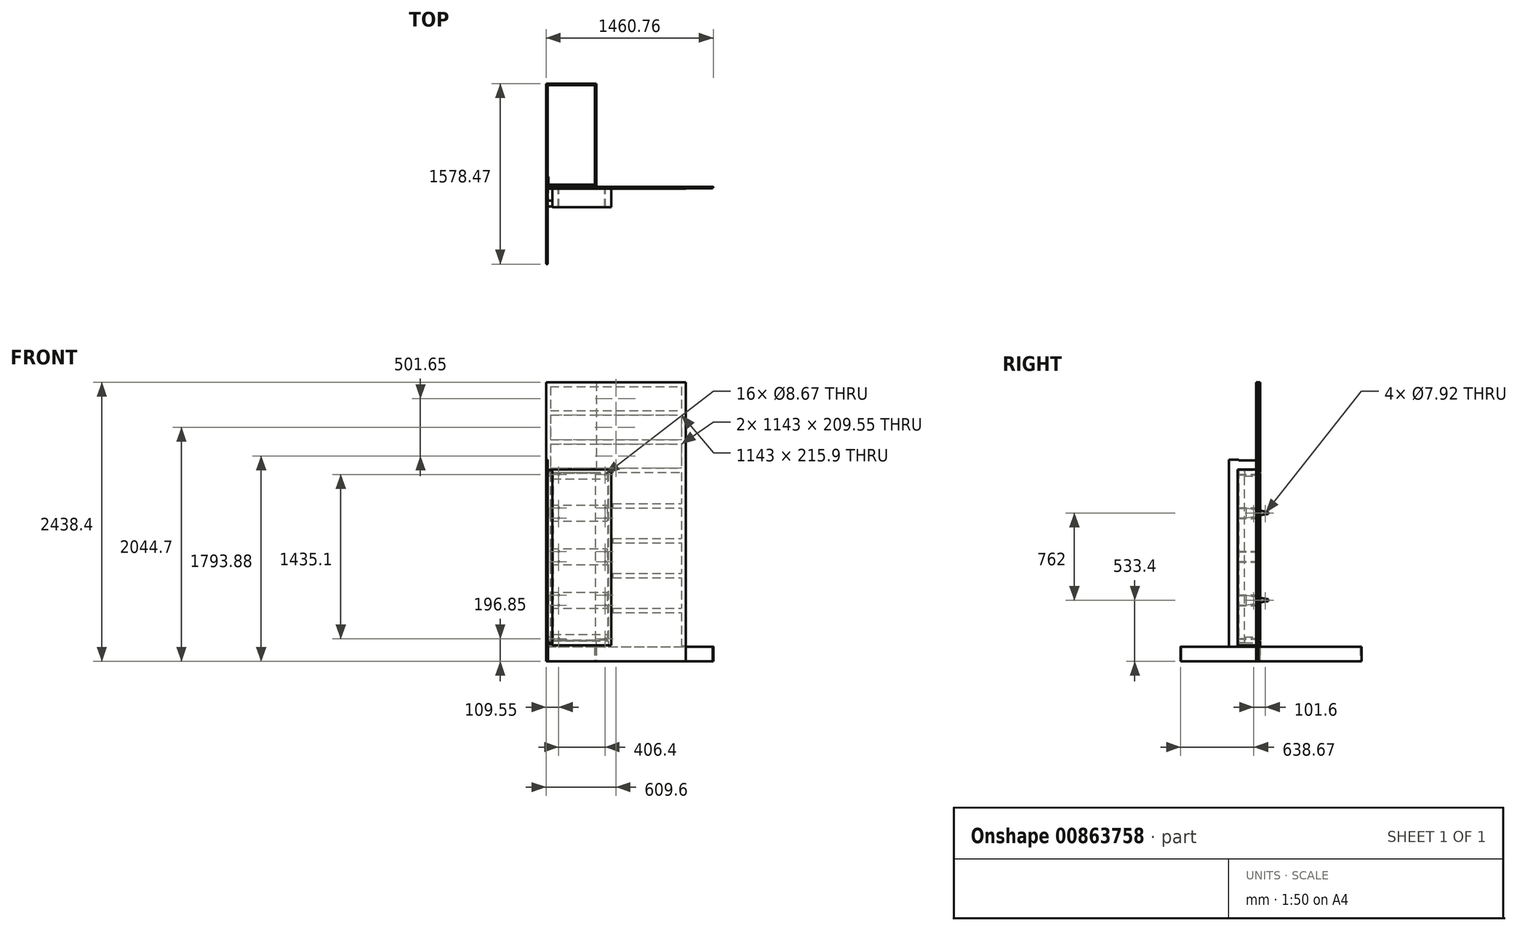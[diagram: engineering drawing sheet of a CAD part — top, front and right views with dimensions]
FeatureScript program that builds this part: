
annotation { "Feature Type Name" : "Feature", "Feature Type Description" : "" }
export const myFeature = defineFeature(function(context is Context, id is Id, definition is map)
    precondition{}
    {
        {
            var Q0;
            Q0=qCreatedBy(makeId("Top.planeOp"),FACE);
            var sketch = newSketch(context, id + "F0", { "sketchPlane" : qUnion([Q0])});
            skLineSegment(sketch, "E0", {"start": v(0, -673.1) * mm, "end": v(0, 901.7) * mm});
            skLineSegment(sketch, "E1", {"start": v(0, 901.7) * mm, "end": v(438.15, 901.7) * mm});
            skLineSegment(sketch, "E2", {"start": v(438.15, 901.7) * mm, "end": v(438.15, 0) * mm});
            skLineSegment(sketch, "E3", {"start": v(438.15, 0) * mm, "end": v(1454.15, 0) * mm});
            skLineSegment(sketch, "E4.0", {"start": v(552.45, 114.3) * mm, "end": v(1454.15, 114.3) * mm});
            skLineSegment(sketch, "E4.1", {"start": v(552.45, 1016) * mm, "end": v(552.45, 114.3) * mm});
            skLineSegment(sketch, "E4.2", {"start": v(-114.3, 1016) * mm, "end": v(552.45, 1016) * mm});
            skLineSegment(sketch, "E4.3", {"start": v(-114.3, -673.1) * mm, "end": v(-114.3, 1016) * mm});
            skLineSegment(sketch, "E5.0", {"start": v(425.45, -12.7) * mm, "end": v(1454.15, -12.7) * mm});
            skLineSegment(sketch, "E5.1", {"start": v(425.45, 889) * mm, "end": v(425.45, -12.7) * mm});
            skLineSegment(sketch, "E5.2", {"start": v(12.7, 889) * mm, "end": v(425.45, 889) * mm});
            skLineSegment(sketch, "E5.3", {"start": v(12.7, -673.1) * mm, "end": v(12.7, 889) * mm});
            skFitSpline(sketch, "E6", {"points": [v(-114.3, -673.1) * mm, v(0, -673.1) * mm, v(12.7, -673.1) * mm], "startDerivative": vector(215.33, 101.54) * mm, "endDerivative": vector(15.02, 74.43) * mm});
            skFitSpline(sketch, "E7", {"points": [v(1454.15, 114.3) * mm, v(1454.15, 0) * mm, v(1454.15, -12.7) * mm], "startDerivative": vector(-157.16, -195.04) * mm, "endDerivative": vector(-135.93, -152.4) * mm});
            skLineSegment(sketch, "E8.bottom", {"start": v(30.7, -669.3) * mm, "end": v(1447.96, -669.3) * mm, "construction": true});
            skLineSegment(sketch, "E8.top", {"start": v(30.7, -660.4) * mm, "end": v(1447.96, -660.4) * mm, "construction": true});
            skLineSegment(sketch, "E8.left", {"start": v(30.7, -669.3) * mm, "end": v(30.7, -660.4) * mm, "construction": true});
            skLineSegment(sketch, "E8.right", {"start": v(1447.96, -669.3) * mm, "end": v(1447.96, -660.4) * mm, "construction": true});
            skLineSegment(sketch, "E9", {"start": v(27.37, -457.2) * mm, "end": v(1426.84, -457.2) * mm, "construction": true});
            skText(sketch, "E10", { "text": "Clothes\n", "fontName": "OpenSans-Regular.ttf"});
            skText(sketch, "E11", { "text": "Shelf", "fontName": "OpenSans-Regular.ttf"});
            skLineSegment(sketch, "E12", {"start": v(-114.3, 584.2) * mm, "end": v(0, 584.2) * mm, "construction": true});
            skLineSegment(sketch, "E13", {"start": v(-114.3, 177.8) * mm, "end": v(0, 177.8) * mm, "construction": true});
            skLineSegment(sketch, "E14", {"start": v(438.15, 556.05) * mm, "end": v(552.45, 556.05) * mm, "construction": true});
            skLineSegment(sketch, "E15", {"start": v(958.85, 0) * mm, "end": v(958.85, 114.3) * mm, "construction": true});
            const initialGuessF0  = {"E10": [1.1723, -0.49137, 1, 0, 0.01667], "E11": [1.16785, -0.64477, 1, 0, 0.02]};
            skSetInitialGuess(sketch, initialGuessF0);
            skSolve(sketch);
        }
        {
            var Q0;
            Q0=qCreatedBy(makeId("Front.planeOp"),FACE);
            var sketch = newSketch(context, id + "F1", { "sketchPlane" : qUnion([Q0])});
            skLineSegment(sketch, "E16.bottom", {"start": v(0, 0) * mm, "end": v(12.7, 0) * mm, "construction": true});
            skLineSegment(sketch, "E16.top", {"start": v(0, 127) * mm, "end": v(12.7, 127) * mm, "construction": true});
            skLineSegment(sketch, "E16.left", {"start": v(0, 0) * mm, "end": v(0, 127) * mm, "construction": true});
            skLineSegment(sketch, "E16.right", {"start": v(12.7, 0) * mm, "end": v(12.7, 127) * mm, "construction": true});
            skLineSegment(sketch, "E17.bottom", {"start": v(438.15, 0) * mm, "end": v(425.45, 0) * mm, "construction": true});
            skLineSegment(sketch, "E17.top", {"start": v(438.15, 127) * mm, "end": v(425.45, 127) * mm, "construction": true});
            skLineSegment(sketch, "E17.left", {"start": v(438.15, 0) * mm, "end": v(438.15, 127) * mm, "construction": true});
            skLineSegment(sketch, "E17.right", {"start": v(425.45, 0) * mm, "end": v(425.45, 127) * mm, "construction": true});
            skLineSegment(sketch, "E18.bottom", {"start": v(0, 0) * mm, "end": v(438.15, 0) * mm, "construction": true});
            skLineSegment(sketch, "E18.top", {"start": v(0, 2438.4) * mm, "end": v(438.15, 2438.4) * mm, "construction": true});
            skLineSegment(sketch, "E18.left", {"start": v(0, 0) * mm, "end": v(0, 2438.4) * mm, "construction": true});
            skLineSegment(sketch, "E18.right", {"start": v(438.15, 0) * mm, "end": v(438.15, 2438.4) * mm, "construction": true});
            skLineSegment(sketch, "E19", {"start": v(958.85, 0) * mm, "end": v(958.85, 2438.4) * mm, "construction": true});
            skLineSegment(sketch, "E20", {"start": v(565.15, 0) * mm, "end": v(565.15, 2438.4) * mm, "construction": true});
            skSolve(sketch);
        }
        {
            var Q0;
            {var subQ2=sQuery(id+"F0.wireOp",EDGE,"E0");Q0=makeQuery(id+"F0.imprint","IMPRINT",FACE,{"disambiguationData":[TD([[makeQuery(id+"F0.imprint","IMPRINT",EDGE,{"derivedFrom":subQ2}),-1.0]])]});}
            var Q1;
            Q1=sQuery(id+"F0.wireOp",EDGE,"E0");
            var Q2;
            Q2=sQuery(id+"F0.wireOp",EDGE,"E1");
            var Q3;
            Q3=sQuery(id+"F0.wireOp",EDGE,"E2");
            var Q4;
            Q4=sQuery(id+"F0.wireOp",EDGE,"E5.1");
            var Q5;
            Q5=sQuery(id+"F0.wireOp",EDGE,"E5.2");
            var Q6;
            Q6=sQuery(id+"F0.wireOp",EDGE,"E5.3");
            var Q7;
            Q7=sQuery(id+"F0.wireOp",EDGE,"E3");
            var Q8;
            Q8=sQuery(id+"F0.wireOp",EDGE,"E5.0");
            extrude(context, id + "F2", {"entities" : qUnion([Q0]), "surfaceEntities" : qUnion([Q1, Q2, Q3, Q4, Q5, Q6, Q7, Q8]), "depth" : 127 * mm, "offsetDistance" : 25.4 * mm});
        }
        {
            var Q0;
            Q0=qCreatedBy(makeId("Front.planeOp"),FACE);
            cPlane(context, id + "F3", {"entities" : qUnion([Q0]), "cplaneType" : CPlaneType.OFFSET, "offset" : 17.45 * mm, "width" : 152.4 * mm, "height" : 152.4 * mm});
        }
        {
            var Q0;
            Q0=qCreatedBy(id+"F3.planeOp",FACE);
            var sketch = newSketch(context, id + "F4", { "sketchPlane" : qUnion([Q0])});
            skLineSegment(sketch, "E21.bottom", {"start": v(55.58, 139.7) * mm, "end": v(569.93, 139.7) * mm});
            skLineSegment(sketch, "E21.top", {"start": v(55.58, 1676.4) * mm, "end": v(569.93, 1676.4) * mm});
            skLineSegment(sketch, "E21.left", {"start": v(55.58, 139.7) * mm, "end": v(55.58, 1676.4) * mm});
            skLineSegment(sketch, "E21.right", {"start": v(569.93, 139.7) * mm, "end": v(569.93, 1676.4) * mm});
            skLineSegment(sketch, "E22", {"start": v(55.58, 1295.4) * mm, "end": v(569.93, 1295.4) * mm});
            skLineSegment(sketch, "E23", {"start": v(55.58, 914.4) * mm, "end": v(569.93, 914.4) * mm});
            skLineSegment(sketch, "E24", {"start": v(55.58, 533.4) * mm, "end": v(569.93, 533.4) * mm});
            skLineSegment(sketch, "E25", {"start": v(55.58, 152.4) * mm, "end": v(569.93, 152.4) * mm, "construction": true});
            skCircle(sketch, "E26", {"center": v(109.55, 1631.95) * mm, "radius": 4.33 * mm});
            skCircle(sketch, "E27", {"center": v(109.55, 1339.85) * mm, "radius": 4.33 * mm});
            skCircle(sketch, "E28", {"center": v(109.55, 1250.95) * mm, "radius": 4.33 * mm});
            skCircle(sketch, "E29", {"center": v(109.55, 958.85) * mm, "radius": 4.33 * mm});
            skCircle(sketch, "E30", {"center": v(109.55, 869.95) * mm, "radius": 4.33 * mm});
            skCircle(sketch, "E31", {"center": v(109.55, 577.85) * mm, "radius": 4.33 * mm});
            skCircle(sketch, "E32", {"center": v(109.55, 488.95) * mm, "radius": 4.33 * mm});
            skCircle(sketch, "E33", {"center": v(109.55, 196.85) * mm, "radius": 4.33 * mm});
            skLineSegment(sketch, "E34", {"start": v(109.55, 1631.95) * mm, "end": v(109.55, 196.85) * mm, "construction": true});
            skCircle(sketch, "E35", {"center": v(515.95, 1631.95) * mm, "radius": 4.33 * mm});
            skCircle(sketch, "E36", {"center": v(515.95, 1339.85) * mm, "radius": 4.33 * mm});
            skCircle(sketch, "E37", {"center": v(515.95, 1250.95) * mm, "radius": 4.33 * mm});
            skCircle(sketch, "E38", {"center": v(515.95, 958.85) * mm, "radius": 4.33 * mm});
            skCircle(sketch, "E39", {"center": v(515.95, 869.95) * mm, "radius": 4.33 * mm});
            skCircle(sketch, "E40", {"center": v(515.95, 577.85) * mm, "radius": 4.33 * mm});
            skCircle(sketch, "E41", {"center": v(515.95, 488.95) * mm, "radius": 4.33 * mm});
            skCircle(sketch, "E42", {"center": v(515.95, 196.85) * mm, "radius": 4.33 * mm});
            skLineSegment(sketch, "E43", {"start": v(515.95, 1631.95) * mm, "end": v(515.95, 196.85) * mm, "construction": true});
            skLineSegment(sketch, "E44", {"start": v(109.55, 1631.95) * mm, "end": v(515.95, 1631.95) * mm, "construction": true});
            skLineSegment(sketch, "E45", {"start": v(109.55, 196.85) * mm, "end": v(515.95, 196.85) * mm, "construction": true});
            skLineSegment(sketch, "E46", {"start": v(109.55, 488.95) * mm, "end": v(515.95, 488.95) * mm, "construction": true});
            skLineSegment(sketch, "E47", {"start": v(109.55, 577.85) * mm, "end": v(515.95, 577.85) * mm, "construction": true});
            skLineSegment(sketch, "E48", {"start": v(109.55, 869.95) * mm, "end": v(515.95, 869.95) * mm, "construction": true});
            skLineSegment(sketch, "E49", {"start": v(109.55, 958.85) * mm, "end": v(515.95, 958.85) * mm, "construction": true});
            skLineSegment(sketch, "E50", {"start": v(109.55, 1250.95) * mm, "end": v(515.95, 1250.95) * mm, "construction": true});
            skLineSegment(sketch, "E51", {"start": v(109.55, 1339.85) * mm, "end": v(515.95, 1339.85) * mm, "construction": true});
            skSolve(sketch);
        }
        {
            var Q0;
            Q0=qCreatedBy(makeId("Front.planeOp"),FACE);
            var Q1;
            Q1 = qBodyType(qCreatedBy(id + "F13" ,EDGE), BodyType.WIRE);
            cPlane(context, id + "F5", {"entities" : qUnion([Q0, Q1]), "cplaneType" : CPlaneType.OFFSET, "offset" : 12.7 * mm, "width" : 152.4 * mm, "height" : 152.4 * mm});
        }
        {
            var Q0;
            Q0=qCreatedBy(id+"F5.planeOp",FACE);
            var sketch = newSketch(context, id + "F6", { "sketchPlane" : qUnion([Q0])});
            skLineSegment(sketch, "E52", {"start": v(3.17, 177.8) * mm, "end": v(3.18, 130.18) * mm});
            skLineSegment(sketch, "E53", {"start": v(3.18, 130.18) * mm, "end": v(15.87, 130.18) * mm});
            skLineSegment(sketch, "E54", {"start": v(15.87, 130.18) * mm, "end": v(15.88, 0) * mm});
            skLineSegment(sketch, "E55", {"start": v(15.87, 0) * mm, "end": v(1219.2, 0) * mm});
            skLineSegment(sketch, "E56", {"start": v(1219.2, 0) * mm, "end": v(1219.2, 2438.4) * mm});
            skLineSegment(sketch, "E57", {"start": v(1219.2, 2438.4) * mm, "end": v(0, 2438.4) * mm});
            skLineSegment(sketch, "E58", {"start": v(0, 2438.4) * mm, "end": v(0, 1651) * mm});
            skLineSegment(sketch, "E59", {"start": v(0, 1651) * mm, "end": v(544.53, 1651) * mm});
            skLineSegment(sketch, "E60", {"start": v(544.53, 1651) * mm, "end": v(544.53, 177.8) * mm});
            skLineSegment(sketch, "E61", {"start": v(544.53, 177.8) * mm, "end": v(3.17, 177.8) * mm});
            skSolve(sketch);
        }
        {
            var Q0;
            Q0=makeQuery(id+"F6.imprint","IMPRINT",FACE,{"disambiguationData":[TD([[makeQuery(id+"F6.imprint","IMPRINT",EDGE,{"derivedFrom":sQuery(id+"F6.wireOp",EDGE,"E52")}),1.0]])]});
            extrude(context, id + "F7", {"entities" : qUnion([Q0]), "depth" : 4.75 * mm, "offsetDistance" : 25.4 * mm});
        }
        {
            var Q0;
            Q0=qCreatedBy(id+"F5.planeOp",FACE);
            var sketch = newSketch(context, id + "F8", { "sketchPlane" : qUnion([Q0])});
            skLineSegment(sketch, "E62.bottom", {"start": v(1219.2, 2438.4) * mm, "end": v(1181.1, 2438.4) * mm});
            skLineSegment(sketch, "E62.top", {"start": v(1219.2, 133.35) * mm, "end": v(1181.1, 133.35) * mm});
            skLineSegment(sketch, "E62.left", {"start": v(1219.2, 2438.4) * mm, "end": v(1219.2, 133.35) * mm});
            skLineSegment(sketch, "E62.right", {"start": v(1181.1, 2438.4) * mm, "end": v(1181.1, 133.35) * mm});
            skLineSegment(sketch, "E63.bottom", {"start": v(38.1, 1689.1) * mm, "end": v(1181.1, 1689.1) * mm});
            skLineSegment(sketch, "E63.top", {"start": v(38.1, 1651) * mm, "end": v(1181.1, 1651) * mm});
            skLineSegment(sketch, "E63.right", {"start": v(1181.1, 1689.1) * mm, "end": v(1181.1, 1651) * mm});
            skLineSegment(sketch, "E64.bottom", {"start": v(38.1, 1936.75) * mm, "end": v(1181.1, 1936.75) * mm});
            skLineSegment(sketch, "E64.top", {"start": v(38.1, 1898.65) * mm, "end": v(1181.1, 1898.65) * mm});
            skLineSegment(sketch, "E64.left", {"start": v(38.1, 1936.75) * mm, "end": v(38.1, 1898.65) * mm});
            skLineSegment(sketch, "E64.right", {"start": v(1181.1, 1936.75) * mm, "end": v(1181.1, 1898.65) * mm});
            skLineSegment(sketch, "E65.bottom", {"start": v(38.1, 2190.75) * mm, "end": v(1181.1, 2190.75) * mm});
            skLineSegment(sketch, "E65.top", {"start": v(38.1, 2152.65) * mm, "end": v(1181.1, 2152.65) * mm});
            skLineSegment(sketch, "E65.left", {"start": v(38.1, 2190.75) * mm, "end": v(38.1, 2152.65) * mm});
            skLineSegment(sketch, "E65.right", {"start": v(1181.1, 2190.75) * mm, "end": v(1181.1, 2152.65) * mm});
            skLineSegment(sketch, "E66.bottom", {"start": v(38.1, 2438.4) * mm, "end": v(1181.1, 2438.4) * mm});
            skLineSegment(sketch, "E66.top", {"start": v(38.1, 2400.3) * mm, "end": v(1181.1, 2400.3) * mm});
            skLineSegment(sketch, "E66.left", {"start": v(38.1, 2438.4) * mm, "end": v(38.1, 2400.3) * mm});
            skLineSegment(sketch, "E66.right", {"start": v(1181.1, 2438.4) * mm, "end": v(1181.1, 2400.3) * mm});
            skLineSegment(sketch, "E67.bottom", {"start": v(582.63, 1377.95) * mm, "end": v(1181.1, 1377.95) * mm});
            skLineSegment(sketch, "E67.top", {"start": v(582.63, 1339.85) * mm, "end": v(1181.1, 1339.85) * mm});
            skLineSegment(sketch, "E67.left", {"start": v(582.63, 1377.95) * mm, "end": v(582.63, 1339.85) * mm});
            skLineSegment(sketch, "E67.right", {"start": v(1181.1, 1377.95) * mm, "end": v(1181.1, 1339.85) * mm});
            skLineSegment(sketch, "E68.bottom", {"start": v(544.53, 1651) * mm, "end": v(582.63, 1651) * mm});
            skLineSegment(sketch, "E68.top", {"start": v(544.53, 133.35) * mm, "end": v(582.63, 133.35) * mm});
            skLineSegment(sketch, "E68.left", {"start": v(544.53, 1651) * mm, "end": v(544.53, 133.35) * mm});
            skLineSegment(sketch, "E68.right", {"start": v(582.63, 1651) * mm, "end": v(582.63, 133.35) * mm});
            skLineSegment(sketch, "E69.bottom", {"start": v(582.63, 1073.15) * mm, "end": v(1181.1, 1073.15) * mm});
            skLineSegment(sketch, "E69.top", {"start": v(582.63, 1035.05) * mm, "end": v(1181.1, 1035.05) * mm});
            skLineSegment(sketch, "E69.left", {"start": v(582.63, 1073.15) * mm, "end": v(582.63, 1035.05) * mm});
            skLineSegment(sketch, "E69.right", {"start": v(1181.1, 1073.15) * mm, "end": v(1181.1, 1035.05) * mm});
            skLineSegment(sketch, "E70.bottom", {"start": v(582.63, 768.35) * mm, "end": v(1181.1, 768.35) * mm});
            skLineSegment(sketch, "E70.top", {"start": v(582.63, 730.25) * mm, "end": v(1181.1, 730.25) * mm});
            skLineSegment(sketch, "E70.left", {"start": v(582.63, 768.35) * mm, "end": v(582.63, 730.25) * mm});
            skLineSegment(sketch, "E70.right", {"start": v(1181.1, 768.35) * mm, "end": v(1181.1, 730.25) * mm});
            skLineSegment(sketch, "E71.bottom", {"start": v(582.63, 463.55) * mm, "end": v(1181.1, 463.55) * mm});
            skLineSegment(sketch, "E71.top", {"start": v(582.63, 425.45) * mm, "end": v(1181.1, 425.45) * mm});
            skLineSegment(sketch, "E71.left", {"start": v(582.63, 463.55) * mm, "end": v(582.63, 425.45) * mm});
            skLineSegment(sketch, "E71.right", {"start": v(1181.1, 463.55) * mm, "end": v(1181.1, 425.45) * mm});
            skLineSegment(sketch, "E72.bottom", {"start": v(15.88, 127) * mm, "end": v(422.28, 127) * mm});
            skLineSegment(sketch, "E72.top", {"start": v(15.88, 0) * mm, "end": v(422.28, 0) * mm});
            skLineSegment(sketch, "E72.left", {"start": v(15.87, 127) * mm, "end": v(15.87, 0) * mm});
            skLineSegment(sketch, "E72.right", {"start": v(422.28, 127) * mm, "end": v(422.28, 0) * mm});
            skLineSegment(sketch, "E73.bottom", {"start": v(3.18, 177.8) * mm, "end": v(544.53, 177.8) * mm});
            skLineSegment(sketch, "E73.top", {"start": v(3.18, 139.7) * mm, "end": v(544.53, 139.7) * mm});
            skLineSegment(sketch, "E73.left", {"start": v(3.17, 177.8) * mm, "end": v(3.18, 139.7) * mm});
            skLineSegment(sketch, "E73.right", {"start": v(544.53, 177.8) * mm, "end": v(544.53, 139.7) * mm});
            skLineSegment(sketch, "E74.bottom", {"start": v(0, 2438.4) * mm, "end": v(38.1, 2438.4) * mm});
            skLineSegment(sketch, "E74.top", {"start": v(0, 1651) * mm, "end": v(38.1, 1651) * mm});
            skLineSegment(sketch, "E74.left", {"start": v(0, 2438.4) * mm, "end": v(0, 1651) * mm});
            skLineSegment(sketch, "E74.right", {"start": v(38.1, 2438.4) * mm, "end": v(38.1, 1651) * mm});
            skLineSegment(sketch, "E75", {"start": v(38.1, 1689.1) * mm, "end": v(38.1, 1651) * mm});
            skSolve(sketch);
        }
        {
            var Q0;
            Q0=qCreatedBy(makeId("Top.planeOp"),FACE);
            cPlane(context, id + "F9", {"entities" : qUnion([Q0]), "cplaneType" : CPlaneType.OFFSET, "offset" : 1524 * mm, "width" : 152.4 * mm, "height" : 152.4 * mm});
        }
        {
            var Q0;
            Q0=qCreatedBy(id+"F9.planeOp",FACE);
            var sketch = newSketch(context, id + "F10", { "sketchPlane" : qUnion([Q0])});
            skLineSegment(sketch, "E76.bottom", {"start": v(0, -107.95) * mm, "end": v(19.05, -107.95) * mm});
            skLineSegment(sketch, "E76.top", {"start": v(0, 704.85) * mm, "end": v(19.05, 704.85) * mm});
            skLineSegment(sketch, "E76.left", {"start": v(0, -107.95) * mm, "end": v(0, 704.85) * mm});
            skLineSegment(sketch, "E76.right", {"start": v(19.05, -107.95) * mm, "end": v(19.05, 704.85) * mm});
            skLineSegment(sketch, "E77.bottom", {"start": v(19.05, 87.31) * mm, "end": v(21.59, 87.31) * mm});
            skLineSegment(sketch, "E77.top", {"start": v(19.05, -158.75) * mm, "end": v(21.6, -158.75) * mm});
            skLineSegment(sketch, "E77.left", {"start": v(19.05, 87.31) * mm, "end": v(19.05, -158.75) * mm});
            skLineSegment(sketch, "E77.right", {"start": v(21.59, 87.31) * mm, "end": v(21.6, -158.75) * mm});
            skLineSegment(sketch, "E78", {"start": v(19.05, -158.75) * mm, "end": v(26.99, -158.75) * mm, "construction": true});
            skCircle(sketch, "E79", {"center": v(26.99, -158.75) * mm, "radius": 2.8 * mm});
            skCircle(sketch, "E80", {"center": v(26.99, -158.75) * mm, "radius": 7.94 * mm});
            skLineSegment(sketch, "E81.bottom", {"start": v(0, -254) * mm, "end": v(12.7, -254) * mm});
            skLineSegment(sketch, "E81.top", {"start": v(0, -171.45) * mm, "end": v(12.7, -171.45) * mm});
            skLineSegment(sketch, "E81.left", {"start": v(0, -171.45) * mm, "end": v(0, -254) * mm});
            skLineSegment(sketch, "E81.right", {"start": v(12.7, -171.45) * mm, "end": v(12.7, -254) * mm});
            skCircle(sketch, "E82", {"center": v(26.99, -158.75) * mm, "radius": 24.8 * mm, "construction": true});
            skLineSegment(sketch, "E83", {"start": v(-131.72, -179.39) * mm, "end": v(182.58, -179.39) * mm, "construction": true});
            skLineSegment(sketch, "E84.bottom", {"start": v(544.53, 0) * mm, "end": v(582.63, 0) * mm});
            skLineSegment(sketch, "E84.top", {"start": v(544.53, -12.7) * mm, "end": v(582.63, -12.7) * mm});
            skLineSegment(sketch, "E84.left", {"start": v(544.53, -12.7) * mm, "end": v(544.53, 0) * mm});
            skLineSegment(sketch, "E84.right", {"start": v(582.63, -12.7) * mm, "end": v(582.63, 0) * mm});
            skLineSegment(sketch, "E85.bottom", {"start": v(1181.1, -12.7) * mm, "end": v(1219.2, -12.7) * mm});
            skLineSegment(sketch, "E85.top", {"start": v(1181.1, 0) * mm, "end": v(1219.2, 0) * mm});
            skLineSegment(sketch, "E85.left", {"start": v(1181.1, -12.7) * mm, "end": v(1181.1, 0) * mm});
            skLineSegment(sketch, "E85.right", {"start": v(1219.2, -12.7) * mm, "end": v(1219.2, 0) * mm});
            skLineSegment(sketch, "E86.bottom", {"start": v(582.63, 0) * mm, "end": v(1181.1, 0) * mm});
            skLineSegment(sketch, "E86.top", {"start": v(582.63, -12.7) * mm, "end": v(1181.1, -12.7) * mm});
            skLineSegment(sketch, "E86.left", {"start": v(582.63, 0) * mm, "end": v(582.63, -12.7) * mm});
            skLineSegment(sketch, "E86.right", {"start": v(1181.1, 0) * mm, "end": v(1181.1, -12.7) * mm});
            skLineSegment(sketch, "E87.bottom", {"start": v(544.53, -12.7) * mm, "end": v(1219.2, -12.7) * mm});
            skLineSegment(sketch, "E87.top", {"start": v(544.53, -17.45) * mm, "end": v(1219.2, -17.45) * mm});
            skLineSegment(sketch, "E87.left", {"start": v(544.53, -12.7) * mm, "end": v(544.53, -17.45) * mm});
            skLineSegment(sketch, "E87.right", {"start": v(1219.2, -12.7) * mm, "end": v(1219.2, -17.45) * mm});
            skSolve(sketch);
        }
        {
            var Q0;
            Q0=qCreatedBy(makeId("Top.planeOp"),FACE);
            cPlane(context, id + "F11", {"entities" : qUnion([Q0]), "cplaneType" : CPlaneType.OFFSET, "offset" : 1668.48 * mm, "width" : 152.4 * mm, "height" : 152.4 * mm});
        }
        {
            var Q0;
            Q0 = qSketchRegion(id + "F4", true);
            extrude(context, id + "F12", {"entities" : qUnion([Q0]), "depth" : 161.92 * mm, "offsetDistance" : 25.4 * mm});
        }
        {
            var Q0;
            Q0=qCreatedBy(id+"F3.planeOp",FACE);
            var sketch = newSketch(context, id + "F13", { "sketchPlane" : qUnion([Q0])});
            skLineSegment(sketch, "E88.0", {"start": v(538.18, 184.15) * mm, "end": v(61.93, 184.15) * mm});
            skLineSegment(sketch, "E88.1", {"start": v(538.18, 1644.65) * mm, "end": v(538.18, 184.15) * mm});
            skLineSegment(sketch, "E88.2", {"start": v(61.93, 1644.65) * mm, "end": v(538.18, 1644.65) * mm});
            skLineSegment(sketch, "E89", {"start": v(61.93, 1644.65) * mm, "end": v(61.93, 184.15) * mm});
            skSolve(sketch);
        }
        {
            var Q0;
            Q0=qCreatedBy(id+"F11.planeOp",FACE);
            var sketch = newSketch(context, id + "F14", { "sketchPlane" : qUnion([Q0])});
            skLineSegment(sketch, "E90.bottom", {"start": v(55.58, -17.45) * mm, "end": v(569.93, -17.45) * mm});
            skLineSegment(sketch, "E90.top", {"start": v(55.58, -179.37) * mm, "end": v(569.93, -179.37) * mm});
            skLineSegment(sketch, "E90.left", {"start": v(55.58, -17.45) * mm, "end": v(55.58, -179.37) * mm});
            skLineSegment(sketch, "E91.bottom", {"start": v(34.93, -158.75) * mm, "end": v(32.39, -158.75) * mm});
            skLineSegment(sketch, "E91.top", {"start": v(34.92, 86.78) * mm, "end": v(32.39, 86.78) * mm});
            skLineSegment(sketch, "E91.left", {"start": v(34.93, -158.75) * mm, "end": v(34.93, 86.78) * mm});
            skLineSegment(sketch, "E91.right", {"start": v(32.39, -158.75) * mm, "end": v(32.39, 86.78) * mm});
            skLineSegment(sketch, "E92", {"start": v(34.93, -158.75) * mm, "end": v(26.99, -158.75) * mm, "construction": true});
            skLineSegment(sketch, "E93.bottom", {"start": v(7.14, -171.45) * mm, "end": v(55.58, -171.45) * mm});
            skLineSegment(sketch, "E93.top", {"start": v(4.78, -120.65) * mm, "end": v(55.58, -120.65) * mm});
            skLineSegment(sketch, "E93.left", {"start": v(4.78, -169.09) * mm, "end": v(4.78, -120.65) * mm});
            skLineSegment(sketch, "E93.right", {"start": v(55.58, -171.45) * mm, "end": v(55.58, -120.65) * mm});
            skLineSegment(sketch, "E94", {"start": v(38.92, -168.27) * mm, "end": v(-16.3, -168.27) * mm, "construction": true});
            skLineSegment(sketch, "E95.bottom", {"start": v(34.92, 0) * mm, "end": v(428.63, 0) * mm});
            skLineSegment(sketch, "E95.top", {"start": v(34.92, 19.05) * mm, "end": v(428.63, 19.05) * mm});
            skLineSegment(sketch, "E95.left", {"start": v(34.93, 0) * mm, "end": v(34.93, 19.05) * mm});
            skLineSegment(sketch, "E95.right", {"start": v(428.63, 0) * mm, "end": v(428.63, 19.05) * mm});
            skPoint(sketch, "E96.visualSharp", {"position": v(4.78, -171.45) * mm});
            skArc(sketch, "E96.filletArc", {"start": v(4.78, -169.09) * mm, "mid": v(5.47, -170.76) * mm, "end": v(7.14, -171.45) * mm});
            skCircle(sketch, "E97", {"center": v(26.99, -158.75) * mm, "radius": 44.1 * mm, "construction": true});
            skLineSegment(sketch, "E98.bottom", {"start": v(26.83, -127.8) * mm, "end": v(32.38, -127.8) * mm});
            skLineSegment(sketch, "E98.left", {"start": v(26.83, -127.8) * mm, "end": v(26.83, 24.6) * mm});
            skLineSegment(sketch, "E99.bottom", {"start": v(26.83, 24.6) * mm, "end": v(230.03, 24.6) * mm});
            skLineSegment(sketch, "E99.right", {"start": v(230.03, 24.6) * mm, "end": v(230.03, 19.05) * mm});
            skLineSegment(sketch, "E100.0", {"start": v(32.38, 19.05) * mm, "end": v(230.03, 19.05) * mm});
            skLineSegment(sketch, "E100.1", {"start": v(32.38, -127.8) * mm, "end": v(32.38, 19.05) * mm});
            skLineSegment(sketch, "E101", {"start": v(29.01, -139.7) * mm, "end": v(52.14, -139.7) * mm, "construction": true});
            skArc(sketch, "E102", {"start": v(428.62, 19.05) * mm, "mid": v(438.67, -5.65) * mm, "end": v(447.2, -30.91) * mm, "construction": true});
            skLineSegment(sketch, "E103", {"start": v(569.93, -17.45) * mm, "end": v(569.93, -179.37) * mm});
            skLineSegment(sketch, "E104.bottom", {"start": v(55.58, 0) * mm, "end": v(535, 0) * mm});
            skLineSegment(sketch, "E104.top", {"start": v(55.58, -12.7) * mm, "end": v(535, -12.7) * mm});
            skLineSegment(sketch, "E104.left", {"start": v(55.58, 0) * mm, "end": v(55.58, -12.7) * mm});
            skLineSegment(sketch, "E104.right", {"start": v(535, 0) * mm, "end": v(535, -12.7) * mm});
            skLineSegment(sketch, "E105.bottom", {"start": v(61.93, -12.7) * mm, "end": v(538.18, -12.7) * mm});
            skLineSegment(sketch, "E105.top", {"start": v(61.93, -17.45) * mm, "end": v(538.18, -17.45) * mm});
            skLineSegment(sketch, "E105.left", {"start": v(61.93, -12.7) * mm, "end": v(61.93, -17.45) * mm});
            skLineSegment(sketch, "E105.right", {"start": v(538.18, -12.7) * mm, "end": v(538.18, -17.45) * mm});
            skArc(sketch, "E106", {"start": v(535, 0) * mm, "mid": v(539.96, -16.86) * mm, "end": v(544.37, -33.87) * mm, "construction": true});
            skLineSegment(sketch, "E107", {"start": v(109.55, -2.05) * mm, "end": v(109.55, -25.34) * mm, "construction": true});
            skLineSegment(sketch, "E108", {"start": v(515.95, -4.13) * mm, "end": v(515.95, -23.15) * mm, "construction": true});
            skSolve(sketch);
        }
        {
            var Q0;
            Q0=qCreatedBy(id+"F3.planeOp",FACE);
            cPlane(context, id + "F15", {"entities" : qUnion([Q0]), "cplaneType" : CPlaneType.OFFSET, "offset" : 17.45 * mm, "oppositeDirection" : true, "width" : 152.4 * mm, "height" : 152.4 * mm});
        }
        {
            var Q0;
            Q0=qCreatedBy(id+"F15.planeOp",FACE);
            var sketch = newSketch(context, id + "F16", { "sketchPlane" : qUnion([Q0])});
            skLineSegment(sketch, "E109.bottom", {"start": v(34.92, 1644.65) * mm, "end": v(428.63, 1644.65) * mm});
            skLineSegment(sketch, "E109.top", {"start": v(34.93, 184.15) * mm, "end": v(428.63, 184.15) * mm});
            skLineSegment(sketch, "E109.left", {"start": v(34.92, 1644.65) * mm, "end": v(34.93, 184.15) * mm});
            skLineSegment(sketch, "E109.right", {"start": v(428.63, 1644.65) * mm, "end": v(428.63, 184.15) * mm});
            skLineSegment(sketch, "E110", {"start": v(34.93, 533.4) * mm, "end": v(428.63, 533.4) * mm, "construction": true});
            skLineSegment(sketch, "E111", {"start": v(34.93, 1295.4) * mm, "end": v(428.63, 1295.4) * mm, "construction": true});
            skSolve(sketch);
        }
        {
            var Q0;
            Q0=qCreatedBy(id+"F15.planeOp",FACE);
            var sketch = newSketch(context, id + "F17", { "sketchPlane" : qUnion([Q0])});
            skLineSegment(sketch, "E112.bottom", {"start": v(55.58, 1644.65) * mm, "end": v(535, 1644.65) * mm});
            skLineSegment(sketch, "E112.top", {"start": v(55.58, 1593.85) * mm, "end": v(535, 1593.85) * mm});
            skLineSegment(sketch, "E112.left", {"start": v(55.58, 1644.65) * mm, "end": v(55.58, 1593.85) * mm});
            skLineSegment(sketch, "E112.right", {"start": v(535, 1644.65) * mm, "end": v(535, 1593.85) * mm});
            skLineSegment(sketch, "E113.bottom", {"start": v(34.93, 603.25) * mm, "end": v(535, 603.25) * mm});
            skLineSegment(sketch, "E113.top", {"start": v(34.93, 463.55) * mm, "end": v(535, 463.55) * mm});
            skLineSegment(sketch, "E113.left", {"start": v(34.93, 603.25) * mm, "end": v(34.93, 463.55) * mm});
            skLineSegment(sketch, "E113.right", {"start": v(535, 603.25) * mm, "end": v(535, 463.55) * mm});
            skLineSegment(sketch, "E114.bottom", {"start": v(55.58, 234.95) * mm, "end": v(535, 234.95) * mm});
            skLineSegment(sketch, "E114.top", {"start": v(55.58, 184.15) * mm, "end": v(535, 184.15) * mm});
            skLineSegment(sketch, "E114.left", {"start": v(55.58, 234.95) * mm, "end": v(55.58, 184.15) * mm});
            skLineSegment(sketch, "E114.right", {"start": v(535, 234.95) * mm, "end": v(535, 184.15) * mm});
            skLineSegment(sketch, "E115.bottom", {"start": v(34.93, 1365.25) * mm, "end": v(535, 1365.25) * mm});
            skLineSegment(sketch, "E115.top", {"start": v(34.93, 1225.55) * mm, "end": v(535, 1225.55) * mm});
            skLineSegment(sketch, "E115.left", {"start": v(34.93, 1365.25) * mm, "end": v(34.93, 1225.55) * mm});
            skLineSegment(sketch, "E115.right", {"start": v(535, 1365.25) * mm, "end": v(535, 1225.55) * mm});
            skLineSegment(sketch, "E116.bottom", {"start": v(34.93, 984.25) * mm, "end": v(535, 984.25) * mm});
            skLineSegment(sketch, "E116.top", {"start": v(34.93, 844.55) * mm, "end": v(535, 844.55) * mm});
            skLineSegment(sketch, "E116.left", {"start": v(34.93, 984.25) * mm, "end": v(34.93, 844.55) * mm});
            skLineSegment(sketch, "E116.right", {"start": v(535, 984.25) * mm, "end": v(535, 844.55) * mm});
            skLineSegment(sketch, "E117.bottom", {"start": v(55.58, 1668.48) * mm, "end": v(4.78, 1668.48) * mm});
            skLineSegment(sketch, "E117.top", {"start": v(55.58, 1617.68) * mm, "end": v(4.78, 1617.68) * mm});
            skLineSegment(sketch, "E117.left", {"start": v(55.58, 1668.48) * mm, "end": v(55.58, 1617.68) * mm});
            skLineSegment(sketch, "E117.right", {"start": v(4.78, 1668.48) * mm, "end": v(4.78, 1617.68) * mm});
            skLineSegment(sketch, "E118.bottom", {"start": v(55.58, 211.12) * mm, "end": v(4.78, 211.12) * mm});
            skLineSegment(sketch, "E118.top", {"start": v(55.58, 160.32) * mm, "end": v(4.78, 160.32) * mm});
            skLineSegment(sketch, "E118.left", {"start": v(55.58, 211.12) * mm, "end": v(55.58, 160.32) * mm});
            skLineSegment(sketch, "E118.right", {"start": v(4.78, 211.12) * mm, "end": v(4.78, 160.32) * mm});
            skSolve(sketch);
        }
        {
            var Q0;
            Q0 = qSketchRegion(id + "F16", true);
            extrude(context, id + "F18", {"entities" : qUnion([Q0]), "oppositeDirection" : true, "depth" : 19.05 * mm, "offsetDistance" : 25.4 * mm});
        }
        {
            var Q0;
            {var subQ6=sQuery(id+"F14.wireOp",EDGE,"E91.bottom");Q0=makeQuery(id+"F14.imprint","IMPRINT",FACE,{"disambiguationData":[TD([[makeQuery(id+"F14.imprint","IMPRINT",EDGE,{"derivedFrom":subQ6}),1.0]])]});}
            var Q1;
            {var subQ1=sQuery(id+"F14.wireOp",EDGE,"E91.bottom");Q1=makeQuery(id+"F14.imprint","IMPRINT",FACE,{"disambiguationData":[TD([[makeQuery(id+"F14.imprint","IMPRINT",EDGE,{"derivedFrom":subQ1}),-1.0]])]});}
            var Q2;
            {var subQ5=sQuery(id+"F14.wireOp",EDGE,"E98.bottom");Q2=makeQuery(id+"F14.imprint","IMPRINT",FACE,{"disambiguationData":[TD([[makeQuery(id+"F14.imprint","IMPRINT",EDGE,{"derivedFrom":subQ5}),1.0]])]});}
            var Q3;
            Q3=sQuery(id+"F14.wireOp",EDGE,"E93.top");
            var Q4;
            Q4=sQuery(id+"F14.wireOp",EDGE,"E93.right");
            var Q5;
            Q5=sQuery(id+"F14.wireOp",EDGE,"E93.bottom");
            var Q6;
            Q6=sQuery(id+"F14.wireOp",EDGE,"E93.left");
            extrude(context, id + "F19", {"entities" : qUnion([Q0, Q1, Q2]), "surfaceEntities" : qUnion([Q3, Q4, Q5, Q6]), "oppositeDirection" : true, "depth" : 1508.12 * mm, "offsetDistance" : 25.4 * mm});
        }
        {
            var Q0;
            {var subQ3=sQuery(id+"F17.wireOp",EDGE,"E117.bottom");Q0=makeQuery(id+"F17.imprint","IMPRINT",FACE,{"disambiguationData":[TD([[makeQuery(id+"F17.imprint","IMPRINT",EDGE,{"derivedFrom":subQ3}),1.0]])]});}
            var Q1;
            {var subQ3=sQuery(id+"F17.wireOp",EDGE,"E118.bottom");Q1=makeQuery(id+"F17.imprint","IMPRINT",FACE,{"disambiguationData":[TD([[makeQuery(id+"F17.imprint","IMPRINT",EDGE,{"derivedFrom":subQ3}),1.0]])]});}
            var Q2;
            Q2=sQuery(id+"F17.wireOp",EDGE,"E118.bottom");
            var Q3;
            Q3=sQuery(id+"F17.wireOp",EDGE,"E118.right");
            var Q4;
            Q4=sQuery(id+"F17.wireOp",EDGE,"E118.top");
            var Q5;
            Q5=sQuery(id+"F17.wireOp",EDGE,"E118.left");
            var Q6;
            Q6=sQuery(id+"F17.wireOp",EDGE,"E117.right");
            var Q7;
            Q7=sQuery(id+"F17.wireOp",EDGE,"E117.bottom");
            var Q8;
            Q8=sQuery(id+"F17.wireOp",EDGE,"E117.left");
            var Q9;
            Q9=sQuery(id+"F17.wireOp",EDGE,"E117.top");
            var Q10;
            Q10=makeQuery(id+"F19.opExtrude","SWEPT_FACE",FACE,{"disambiguationData":[OSD([sQuery(id+"F14.wireOp",EDGE,"E93.top")])]});
            extrude(context, id + "F20", {"entities" : qUnion([Q0, Q1]), "surfaceEntities" : qUnion([Q2, Q3, Q4, Q5, Q6, Q7, Q8, Q9]), "endBound" : BoundingType.UP_TO_SURFACE, "depth" : 25.4 * mm, "endBoundEntityFace" : qUnion([Q10]), "offsetDistance" : 25.4 * mm});
        }
        {
            var Q0;
            {var subQ2=sQuery(id+"F17.wireOp",EDGE,"E112.bottom");Q0=makeQuery(id+"F17.imprint","IMPRINT",FACE,{"disambiguationData":[TD([[makeQuery(id+"F17.imprint","IMPRINT",EDGE,{"derivedFrom":subQ2}),-1.0]])]});}
            var Q1;
            Q1=makeQuery(id+"F17.imprint","IMPRINT",FACE,{"disambiguationData":[TD([[makeQuery(id+"F17.imprint","IMPRINT",EDGE,{"derivedFrom":sQuery(id+"F17.wireOp",EDGE,"E115.bottom")}),-1.0]])]});
            var Q2;
            Q2=makeQuery(id+"F17.imprint","IMPRINT",FACE,{"disambiguationData":[TD([[makeQuery(id+"F17.imprint","IMPRINT",EDGE,{"derivedFrom":sQuery(id+"F17.wireOp",EDGE,"E116.bottom")}),-1.0]])]});
            var Q3;
            Q3=makeQuery(id+"F17.imprint","IMPRINT",FACE,{"disambiguationData":[TD([[makeQuery(id+"F17.imprint","IMPRINT",EDGE,{"derivedFrom":sQuery(id+"F17.wireOp",EDGE,"E113.bottom")}),-1.0]])]});
            var Q4;
            Q4=makeQuery(id+"F17.imprint","IMPRINT",FACE,{"disambiguationData":[TD([[makeQuery(id+"F17.imprint","IMPRINT",EDGE,{"derivedFrom":sQuery(id+"F17.wireOp",EDGE,"E114.bottom")}),-1.0]])]});
            extrude(context, id + "F21", {"entities" : qUnion([Q0, Q1, Q2, Q3, Q4]), "depth" : 12.7 * mm, "offsetDistance" : 25.4 * mm});
        }
        {
            var Q0;
            Q0=qCreatedBy(makeId("Right.planeOp"),FACE);
            var sketch = newSketch(context, id + "F22", { "sketchPlane" : qUnion([Q0])});
            skLineSegment(sketch, "E119", {"start": v(0, 2438.4) * mm, "end": v(903.42, 2438.4) * mm, "construction": true});
            skLineSegment(sketch, "E120", {"start": v(903.42, 0) * mm, "end": v(903.42, 2438.4) * mm, "construction": true});
            skLineSegment(sketch, "E121.left", {"start": v(-107.95, 1614.51) * mm, "end": v(-107.95, 214.04) * mm});
            skLineSegment(sketch, "E121.right", {"start": v(704.85, 1652.95) * mm, "end": v(704.85, 133.35) * mm});
            skLineSegment(sketch, "E122", {"start": v(903.42, 1295.4) * mm, "end": v(-285.88, 1295.4) * mm, "construction": true});
            skLineSegment(sketch, "E123", {"start": v(903.42, 533.4) * mm, "end": v(-311.78, 533.4) * mm, "construction": true});
            skLineSegment(sketch, "E124.bottom", {"start": v(-254, 1760.55) * mm, "end": v(-171.45, 1760.55) * mm});
            skLineSegment(sketch, "E124.top", {"start": v(-254, 127) * mm, "end": v(-171.45, 127) * mm});
            skLineSegment(sketch, "E124.left", {"start": v(-254, 1760.55) * mm, "end": v(-254, 127) * mm});
            skLineSegment(sketch, "E124.right", {"start": v(-171.45, 1760.55) * mm, "end": v(-171.45, 127) * mm});
            skLineSegment(sketch, "E125.bottom", {"start": v(-171.45, 1754.2) * mm, "end": v(-17.45, 1754.2) * mm});
            skLineSegment(sketch, "E125.top", {"start": v(-171.45, 1671.65) * mm, "end": v(-17.45, 1671.65) * mm});
            skLineSegment(sketch, "E125.left", {"start": v(-171.45, 1754.2) * mm, "end": v(-171.45, 1671.65) * mm});
            skLineSegment(sketch, "E125.right", {"start": v(-17.45, 1754.2) * mm, "end": v(-17.45, 1671.65) * mm});
            skLineSegment(sketch, "E126", {"start": v(584.2, 2438.4) * mm, "end": v(584.2, 0) * mm, "construction": true});
            skLineSegment(sketch, "E127", {"start": v(177.8, 2438.4) * mm, "end": v(177.8, 0) * mm, "construction": true});
            skLineSegment(sketch, "E128", {"start": v(-149.22, 581.02) * mm, "end": v(-149.22, 485.77) * mm});
            skLineSegment(sketch, "E129", {"start": v(-149.23, 485.77) * mm, "end": v(87.31, 523.88) * mm});
            skLineSegment(sketch, "E130", {"start": v(87.31, 523.88) * mm, "end": v(87.31, 542.93) * mm});
            skLineSegment(sketch, "E131", {"start": v(87.31, 542.93) * mm, "end": v(-149.22, 581.03) * mm});
            skLineSegment(sketch, "E132.bottom", {"start": v(-149.22, 581.02) * mm, "end": v(-168.27, 581.02) * mm});
            skLineSegment(sketch, "E132.top", {"start": v(-149.22, 485.77) * mm, "end": v(-168.27, 485.77) * mm});
            skLineSegment(sketch, "E132.left", {"start": v(-149.22, 581.03) * mm, "end": v(-149.22, 485.77) * mm});
            skLineSegment(sketch, "E132.right", {"start": v(-168.27, 581.02) * mm, "end": v(-168.27, 485.77) * mm});
            skLineSegment(sketch, "E133", {"start": v(-158.75, 581.02) * mm, "end": v(-158.75, 485.78) * mm, "construction": true});
            skCircle(sketch, "E134", {"center": v(-38.1, 533.4) * mm, "radius": 3.96 * mm});
            skCircle(sketch, "E135", {"center": v(63.5, 533.4) * mm, "radius": 3.96 * mm});
            skLineSegment(sketch, "E136", {"start": v(-149.22, 1343.02) * mm, "end": v(-149.22, 1247.78) * mm});
            skLineSegment(sketch, "E137", {"start": v(-149.23, 1247.77) * mm, "end": v(87.31, 1285.88) * mm});
            skLineSegment(sketch, "E138", {"start": v(87.31, 1285.88) * mm, "end": v(87.31, 1304.93) * mm});
            skLineSegment(sketch, "E139", {"start": v(87.31, 1304.92) * mm, "end": v(-149.22, 1343.03) * mm});
            skLineSegment(sketch, "E140.bottom", {"start": v(-149.23, 1343.03) * mm, "end": v(-168.28, 1343.03) * mm});
            skLineSegment(sketch, "E140.top", {"start": v(-149.22, 1247.78) * mm, "end": v(-168.28, 1247.78) * mm});
            skLineSegment(sketch, "E140.left", {"start": v(-149.22, 1343.03) * mm, "end": v(-149.22, 1247.78) * mm});
            skLineSegment(sketch, "E140.right", {"start": v(-168.28, 1343.03) * mm, "end": v(-168.28, 1247.78) * mm});
            skLineSegment(sketch, "E141", {"start": v(-158.75, 1343.03) * mm, "end": v(-158.75, 1247.78) * mm, "construction": true});
            skCircle(sketch, "E142", {"center": v(-38.1, 1295.4) * mm, "radius": 3.96 * mm});
            skCircle(sketch, "E143", {"center": v(63.5, 1295.4) * mm, "radius": 3.96 * mm});
            skLineSegment(sketch, "E144", {"start": v(87.31, 1295.4) * mm, "end": v(-168.28, 1295.4) * mm, "construction": true});
            skLineSegment(sketch, "E145.bottom", {"start": v(7.92, 184.15) * mm, "end": v(-17.45, 184.15) * mm});
            skLineSegment(sketch, "E145.top", {"start": v(7.92, 151.53) * mm, "end": v(-17.45, 151.53) * mm});
            skLineSegment(sketch, "E145.left", {"start": v(7.92, 184.15) * mm, "end": v(7.92, 151.53) * mm});
            skLineSegment(sketch, "E145.right", {"start": v(-17.45, 184.15) * mm, "end": v(-17.45, 151.53) * mm});
            skLineSegment(sketch, "E146.bottom", {"start": v(-17.45, 1644.65) * mm, "end": v(4.4, 1644.65) * mm});
            skLineSegment(sketch, "E146.top", {"start": v(-17.45, 1672.6) * mm, "end": v(4.4, 1672.6) * mm});
            skLineSegment(sketch, "E146.left", {"start": v(-17.45, 1644.65) * mm, "end": v(-17.45, 1672.6) * mm});
            skLineSegment(sketch, "E146.right", {"start": v(4.4, 1644.65) * mm, "end": v(4.4, 1672.6) * mm});
            skLineSegment(sketch, "E147", {"start": v(-107.95, 214.04) * mm, "end": v(19.05, 214.04) * mm});
            skLineSegment(sketch, "E148", {"start": v(19.05, 214.04) * mm, "end": v(19.05, 133.35) * mm});
            skLineSegment(sketch, "E149", {"start": v(19.05, 133.35) * mm, "end": v(704.85, 133.35) * mm});
            skLineSegment(sketch, "E150", {"start": v(-107.95, 1614.51) * mm, "end": v(46.38, 1614.51) * mm});
            skLineSegment(sketch, "E151", {"start": v(46.38, 1614.51) * mm, "end": v(46.38, 1652.95) * mm});
            skLineSegment(sketch, "E152", {"start": v(46.38, 1652.95) * mm, "end": v(704.85, 1652.95) * mm});
            skSolve(sketch);
        }
        {
            var Q0;
            {var subQ10=sQuery(id+"F22.wireOp",EDGE,"E121.bottom");Q0=makeQuery(id+"F22.imprint","IMPRINT",FACE,{"disambiguationData":[TD([[makeQuery(id+"F22.imprint","IMPRINT",EDGE,{"derivedFrom":subQ10}),-1.0]])]});}
            var Q1;
            {var subQ0=sQuery(id+"F22.wireOp",EDGE,"E130");Q1=makeQuery(id+"F22.imprint","IMPRINT",FACE,{"disambiguationData":[TD([[makeQuery(id+"F22.imprint","IMPRINT",EDGE,{"derivedFrom":subQ0}),1.0]])]});}
            var Q2;
            {var subQ1=sQuery(id+"F22.wireOp",EDGE,"E138");Q2=makeQuery(id+"F22.imprint","IMPRINT",FACE,{"disambiguationData":[TD([[makeQuery(id+"F22.imprint","IMPRINT",EDGE,{"derivedFrom":subQ1}),1.0]])]});}
            extrude(context, id + "F23", {"entities" : qUnion([Q0, Q1, Q2]), "depth" : 19.05 * mm, "offsetDistance" : 25.4 * mm});
        }
        {
            var Q0;
            Q0=makeQuery(id+"F22.imprint","IMPRINT",FACE,{"disambiguationData":[TD([[makeQuery(id+"F22.imprint","IMPRINT",EDGE,{"derivedFrom":sQuery(id+"F22.wireOp",EDGE,"E125.bottom")}),-1.0]])]});
            var Q1;
            {var subQ1=sQuery(id+"F22.wireOp",EDGE,"E124.bottom");Q1=makeQuery(id+"F22.imprint","IMPRINT",FACE,{"disambiguationData":[TD([[makeQuery(id+"F22.imprint","IMPRINT",EDGE,{"derivedFrom":subQ1}),-1.0]])]});}
            extrude(context, id + "F24", {"entities" : qUnion([Q0, Q1]), "depth" : 15.08 * mm, "offsetDistance" : 25.4 * mm});
        }
        {
            var Q0;
            {var subQ0=sQuery(id+"F8.wireOp",EDGE,"E66.bottom");Q0=makeQuery(id+"F8.imprint","IMPRINT",FACE,{"disambiguationData":[TD([[makeQuery(id+"F8.imprint","IMPRINT",EDGE,{"derivedFrom":subQ0}),-1.0]])]});}
            var Q1;
            {var subQ1=sQuery(id+"F8.wireOp",EDGE,"E74.bottom");Q1=makeQuery(id+"F8.imprint","IMPRINT",FACE,{"disambiguationData":[TD([[makeQuery(id+"F8.imprint","IMPRINT",EDGE,{"derivedFrom":subQ1}),-1.0]])]});}
            var Q2;
            {var subQ0=sQuery(id+"F8.wireOp",EDGE,"E65.bottom");Q2=makeQuery(id+"F8.imprint","IMPRINT",FACE,{"disambiguationData":[TD([[makeQuery(id+"F8.imprint","IMPRINT",EDGE,{"derivedFrom":subQ0}),-1.0]])]});}
            var Q3;
            {var subQ0=sQuery(id+"F8.wireOp",EDGE,"E64.bottom");Q3=makeQuery(id+"F8.imprint","IMPRINT",FACE,{"disambiguationData":[TD([[makeQuery(id+"F8.imprint","IMPRINT",EDGE,{"derivedFrom":subQ0}),-1.0]])]});}
            var Q4;
            Q4=makeQuery(id+"F8.imprint","IMPRINT",FACE,{"disambiguationData":[TD([[makeQuery(id+"F8.imprint","IMPRINT",EDGE,{"derivedFrom":sQuery(id+"F8.wireOp",EDGE,"E63.bottom")}),-1.0]])]});
            var Q5;
            Q5=makeQuery(id+"F8.imprint","IMPRINT",FACE,{"disambiguationData":[TD([[makeQuery(id+"F8.imprint","IMPRINT",EDGE,{"derivedFrom":sQuery(id+"F8.wireOp",EDGE,"E62.bottom")}),1.0]])]});
            var Q6;
            {var subQ0=sQuery(id+"F8.wireOp",EDGE,"E67.bottom");Q6=makeQuery(id+"F8.imprint","IMPRINT",FACE,{"disambiguationData":[TD([[makeQuery(id+"F8.imprint","IMPRINT",EDGE,{"derivedFrom":subQ0}),-1.0]])]});}
            var Q7;
            Q7=makeQuery(id+"F8.imprint","IMPRINT",FACE,{"disambiguationData":[TD([[makeQuery(id+"F8.imprint","IMPRINT",EDGE,{"derivedFrom":sQuery(id+"F8.wireOp",EDGE,"E69.bottom")}),-1.0]])]});
            var Q8;
            Q8=makeQuery(id+"F8.imprint","IMPRINT",FACE,{"disambiguationData":[TD([[makeQuery(id+"F8.imprint","IMPRINT",EDGE,{"derivedFrom":sQuery(id+"F8.wireOp",EDGE,"E73.bottom")}),-1.0]])]});
            var Q9;
            Q9=makeQuery(id+"F8.imprint","IMPRINT",FACE,{"disambiguationData":[TD([[makeQuery(id+"F8.imprint","IMPRINT",EDGE,{"derivedFrom":sQuery(id+"F8.wireOp",EDGE,"E71.bottom")}),-1.0]])]});
            var Q10;
            Q10=makeQuery(id+"F8.imprint","IMPRINT",FACE,{"disambiguationData":[TD([[makeQuery(id+"F8.imprint","IMPRINT",EDGE,{"derivedFrom":sQuery(id+"F8.wireOp",EDGE,"E70.bottom")}),-1.0]])]});
            var Q11;
            {var subQ8=sQuery(id+"F8.wireOp",EDGE,"E68.bottom");Q11=makeQuery(id+"F8.imprint","IMPRINT",FACE,{"disambiguationData":[TD([[makeQuery(id+"F8.imprint","IMPRINT",EDGE,{"derivedFrom":subQ8}),-1.0]])]});}
            extrude(context, id + "F25", {"entities" : qUnion([Q0, Q1, Q2, Q3, Q4, Q5, Q6, Q7, Q8, Q9, Q10, Q11]), "oppositeDirection" : true, "depth" : 12.7 * mm, "offsetDistance" : 25.4 * mm});
        }
        {
            var Q0;
            Q0=makeQuery(id+"F8.imprint","IMPRINT",FACE,{"disambiguationData":[TD([[makeQuery(id+"F8.imprint","IMPRINT",EDGE,{"derivedFrom":sQuery(id+"F8.wireOp",EDGE,"E72.bottom")}),-1.0]])]});
            extrude(context, id + "F26", {"entities" : qUnion([Q0]), "operationType" : NewBodyOperationType.ADD, "oppositeDirection" : true, "depth" : 12.7 * mm, "offsetDistance" : 25.4 * mm});
        }
        {
            var Q0;
            Q0=makeQuery(id+"F13.imprint","IMPRINT",FACE,{"disambiguationData":[TD([[makeQuery(id+"F13.imprint","IMPRINT",EDGE,{"derivedFrom":sQuery(id+"F13.wireOp",EDGE,"E88.0")}),-1.0]])]});
            extrude(context, id + "F27", {"entities" : qUnion([Q0]), "oppositeDirection" : true, "depth" : 4.75 * mm, "offsetDistance" : 25.4 * mm});
        }
        {
            var Q0;
            Q0=qCreatedBy(makeId("Front.planeOp"),FACE);
            var sketch = newSketch(context, id + "F28", { "sketchPlane" : qUnion([Q0])});
            skLineSegment(sketch, "E153.bottom", {"start": v(0, 2438.4) * mm, "end": v(438.15, 2438.4) * mm});
            skLineSegment(sketch, "E153.top", {"start": v(0, 1651) * mm, "end": v(438.15, 1651) * mm});
            skLineSegment(sketch, "E153.left", {"start": v(0, 2438.4) * mm, "end": v(0, 1651) * mm});
            skLineSegment(sketch, "E153.right", {"start": v(438.15, 2438.4) * mm, "end": v(438.15, 1651) * mm});
            skLineSegment(sketch, "E154", {"start": v(3.17, 177.8) * mm, "end": v(3.18, 130.18) * mm});
            skLineSegment(sketch, "E155", {"start": v(3.18, 130.18) * mm, "end": v(15.87, 130.18) * mm});
            skLineSegment(sketch, "E156", {"start": v(15.87, 130.18) * mm, "end": v(15.88, 0) * mm});
            skLineSegment(sketch, "E157", {"start": v(15.88, 0) * mm, "end": v(425.45, 0) * mm});
            skLineSegment(sketch, "E158", {"start": v(425.45, 0) * mm, "end": v(425.45, 127) * mm});
            skLineSegment(sketch, "E159", {"start": v(425.45, 127) * mm, "end": v(438.15, 127) * mm});
            skLineSegment(sketch, "E160", {"start": v(438.15, 127) * mm, "end": v(438.15, 177.8) * mm});
            skLineSegment(sketch, "E161", {"start": v(438.15, 177.8) * mm, "end": v(3.18, 177.8) * mm});
            skSolve(sketch);
        }
        {
            var Q0;
            Q0=makeQuery(id+"F28.imprint","IMPRINT",FACE,{"disambiguationData":[TD([[makeQuery(id+"F28.imprint","IMPRINT",EDGE,{"derivedFrom":sQuery(id+"F28.wireOp",EDGE,"E153.bottom")}),-1.0]])]});
            var Q1;
            Q1=makeQuery(id+"F28.imprint","IMPRINT",FACE,{"disambiguationData":[TD([[makeQuery(id+"F28.imprint","IMPRINT",EDGE,{"derivedFrom":sQuery(id+"F28.wireOp",EDGE,"E154")}),1.0]])]});
            extrude(context, id + "F29", {"entities" : qUnion([Q0, Q1]), "oppositeDirection" : true, "depth" : 19.05 * mm, "offsetDistance" : 25.4 * mm});
        }
        {
            var Q0;
            Q0=makeQuery(id+"F22.imprint","IMPRINT",FACE,{"disambiguationData":[TD([[makeQuery(id+"F22.imprint","IMPRINT",EDGE,{"derivedFrom":sQuery(id+"F22.wireOp",EDGE,"E145.bottom")}),1.0]])]});
            var Q1;
            Q1=makeQuery(id+"F20.opExtrude","SWEPT_FACE",FACE,{"disambiguationData":[OSD([sQuery(id+"F17.wireOp",EDGE,"E118.left")])]});
            extrude(context, id + "F30", {"entities" : qUnion([Q0]), "operationType" : NewBodyOperationType.REMOVE, "endBound" : BoundingType.UP_TO_SURFACE, "depth" : 25.4 * mm, "endBoundEntityFace" : qUnion([Q1]), "offsetDistance" : 25.4 * mm});
        }
        {
            var Q0;
            {var subQ3=sQuery(id+"F22.wireOp",EDGE,"E146.bottom");Q0=makeQuery(id+"F22.imprint","IMPRINT",FACE,{"disambiguationData":[TD([[makeQuery(id+"F22.imprint","IMPRINT",EDGE,{"derivedFrom":subQ3}),1.0]])]});}
            var Q1;
            Q1=makeQuery(id+"F20.opExtrude","SWEPT_FACE",FACE,{"disambiguationData":[OSD([sQuery(id+"F17.wireOp",EDGE,"E117.left")])]});
            extrude(context, id + "F31", {"entities" : qUnion([Q0]), "operationType" : NewBodyOperationType.REMOVE, "endBound" : BoundingType.UP_TO_SURFACE, "depth" : 25.4 * mm, "endBoundEntityFace" : qUnion([Q1]), "offsetDistance" : 25.4 * mm});
        }
    });
